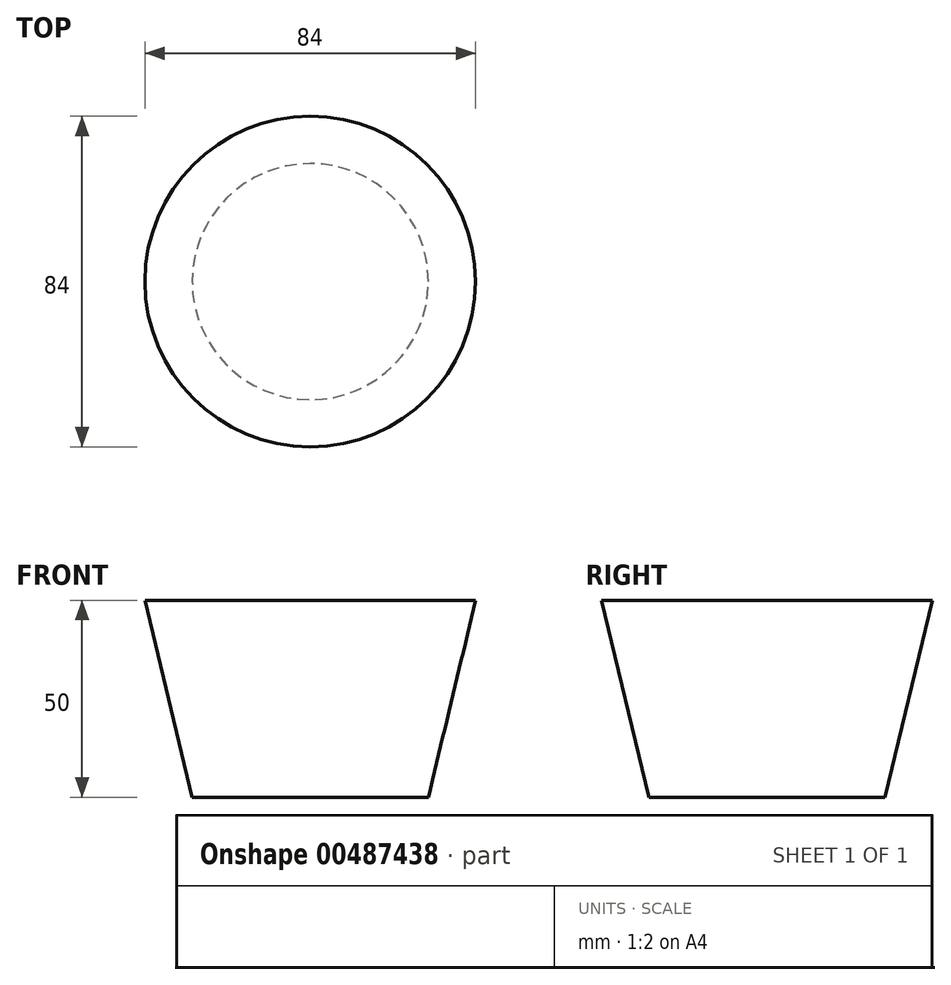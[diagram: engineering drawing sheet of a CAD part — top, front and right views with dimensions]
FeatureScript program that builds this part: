
annotation { "Feature Type Name" : "Feature", "Feature Type Description" : "" }
export const myFeature = defineFeature(function(context is Context, id is Id, definition is map)
    precondition{}
    {
        {
            var Q0;
            Q0=qCreatedBy(makeId("Front.planeOp"),FACE);
            var sketch = newSketch(context, id + "F0", { "sketchPlane" : qUnion([Q0])});
            skLineSegment(sketch, "E0", {"start": v(0, 0) * mm, "end": v(30, 0) * mm});
            skLineSegment(sketch, "E1", {"start": v(30, 0) * mm, "end": v(42, 50) * mm});
            skLineSegment(sketch, "E2", {"start": v(42, 50) * mm, "end": v(0, 50) * mm});
            skLineSegment(sketch, "E3", {"start": v(0, 50) * mm, "end": v(0, 0) * mm});
            skSolve(sketch);
        }
        {
            var Q0;
            Q0=makeQuery(id+"F0.imprint","IMPRINT",FACE,{"disambiguationData":[TD([[makeQuery(id+"F0.imprint","IMPRINT",EDGE,{"derivedFrom":sQuery(id+"F0.wireOp",EDGE,"E0")}),1.0]])]});
            var Q1;
            Q1=sQuery(id+"F0.wireOp",EDGE,"E3");
            revolve(context, id + "F1", {"entities" : qUnion([Q0]), "axis" : qUnion([Q1]), "revolveType" : RevolveType.FULL});
        }
    });
